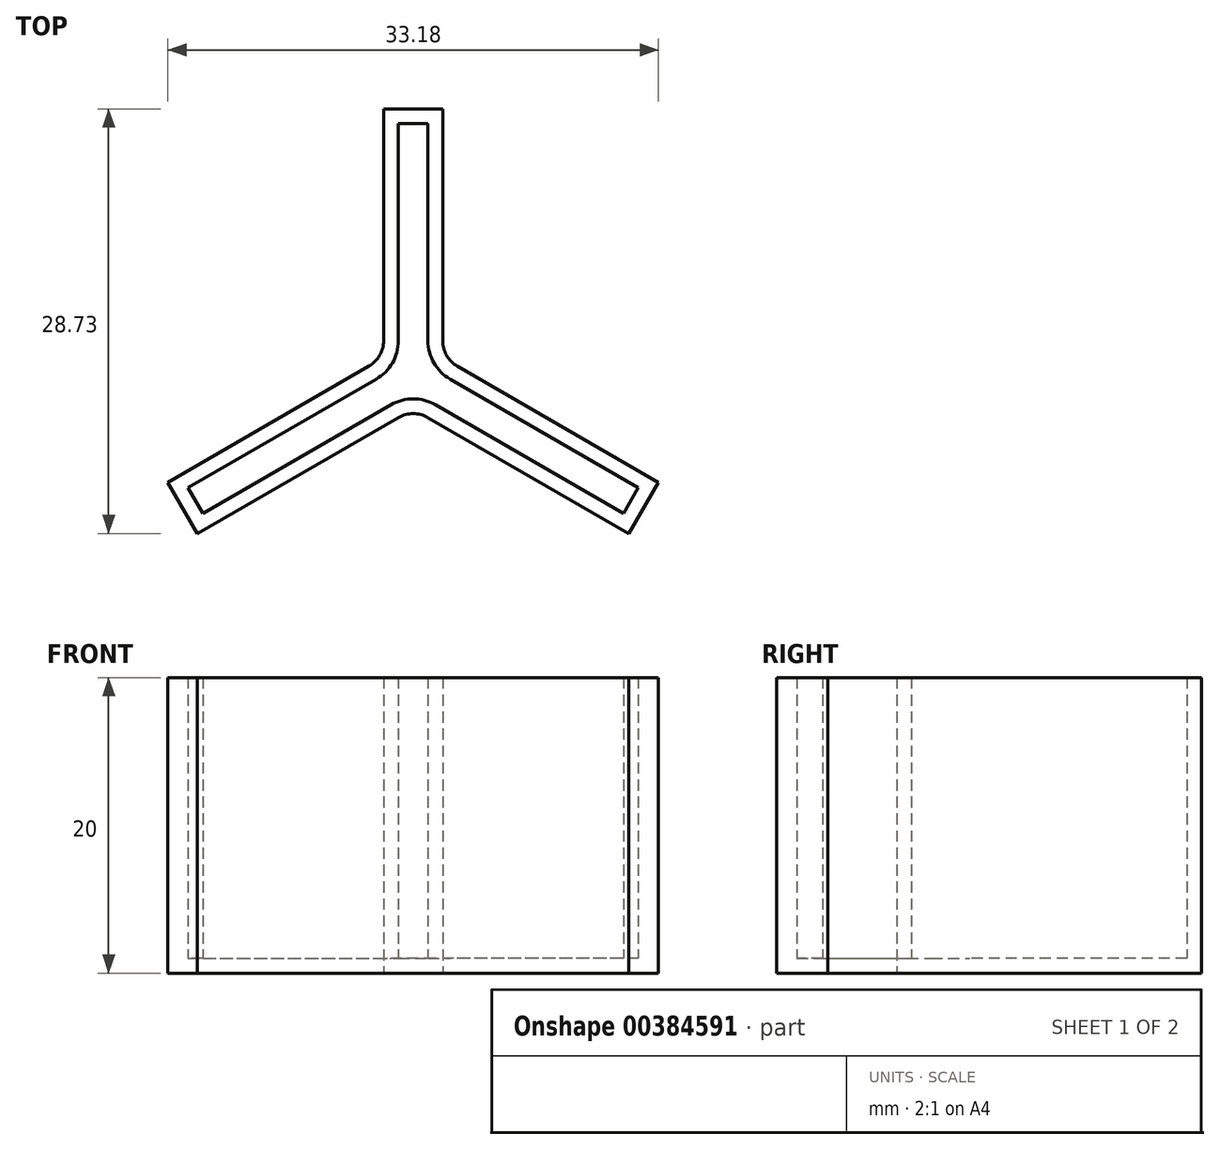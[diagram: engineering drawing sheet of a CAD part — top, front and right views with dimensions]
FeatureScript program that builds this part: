
annotation { "Feature Type Name" : "Feature", "Feature Type Description" : "" }
export const myFeature = defineFeature(function(context is Context, id is Id, definition is map)
    precondition{}
    {
        {
            var Q0;
            Q0=qCreatedBy(makeId("Top.planeOp"),FACE);
            var sketch = newSketch(context, id + "F0", { "sketchPlane" : qUnion([Q0])});
            skLineSegment(sketch, "E0", {"start": v(-1, 17) * mm, "end": v(1, 17) * mm});
            skLineSegment(sketch, "E1", {"start": v(1, 17) * mm, "end": v(1, 2.3) * mm});
            skLineSegment(sketch, "E2.MirrorCS", {"start": v(-1, 17) * mm, "end": v(-1, 2.3) * mm});
            skLineSegment(sketch, "E3.1.0", {"start": v(-14.22, -9.37) * mm, "end": v(-1.5, -2.02) * mm});
            skLineSegment(sketch, "E3.1.1", {"start": v(-14.22, -9.37) * mm, "end": v(-15.22, -7.63) * mm});
            skLineSegment(sketch, "E3.1.2", {"start": v(-15.22, -7.63) * mm, "end": v(-2.5, -0.29) * mm});
            skLineSegment(sketch, "E3.2.0", {"start": v(15.22, -7.63) * mm, "end": v(2.5, -0.29) * mm});
            skLineSegment(sketch, "E3.2.1", {"start": v(15.22, -7.63) * mm, "end": v(14.22, -9.37) * mm});
            skLineSegment(sketch, "E3.2.2", {"start": v(14.22, -9.37) * mm, "end": v(1.5, -2.02) * mm});
            skPoint(sketch, "E3.center", {"position": v(0, 0) * mm});
            skPoint(sketch, "E4.newPointA", {"position": v(-1.5, 2.6) * mm});
            skPoint(sketch, "E4.newPointB", {"position": v(-3, 0) * mm});
            skPoint(sketch, "E5.newPointA", {"position": v(-0.5, 0.87) * mm});
            skPoint(sketch, "E5.newPointB", {"position": v(-1, 0) * mm});
            skArc(sketch, "E5.filletArc", {"start": v(-2.5, -0.29) * mm, "mid": v(-1.4, 0.8) * mm, "end": v(-1, 2.3) * mm});
            skPoint(sketch, "E6.newPointA", {"position": v(1.5, 2.6) * mm});
            skPoint(sketch, "E6.newPointB", {"position": v(3, 0) * mm});
            skPoint(sketch, "E7.newPointA", {"position": v(0.5, 0.87) * mm});
            skPoint(sketch, "E7.newPointB", {"position": v(1, 0) * mm});
            skArc(sketch, "E7.filletArc", {"start": v(1, 2.3) * mm, "mid": v(1.4, 0.8) * mm, "end": v(2.5, -0.29) * mm});
            skPoint(sketch, "E8.newPointA", {"position": v(-0.5, -0.87) * mm});
            skPoint(sketch, "E8.newPointB", {"position": v(0.5, -0.87) * mm});
            skArc(sketch, "E8.filletArc", {"start": v(1.5, -2.02) * mm, "mid": v(0, -1.62) * mm, "end": v(-1.5, -2.02) * mm});
            skPoint(sketch, "E9.newPointA", {"position": v(-1.5, -2.6) * mm});
            skLineSegment(sketch, "E10.0", {"start": v(-14.59, -10.73) * mm, "end": v(-1, -2.89) * mm});
            skArc(sketch, "E11.0", {"start": v(1, -2.89) * mm, "mid": v(0, -2.62) * mm, "end": v(-1, -2.89) * mm});
            skLineSegment(sketch, "E12.0", {"start": v(-14.59, -10.73) * mm, "end": v(-16.59, -7.27) * mm});
            skLineSegment(sketch, "E13.0", {"start": v(-16.59, -7.27) * mm, "end": v(-3, 0.58) * mm});
            skLineSegment(sketch, "E14.1.0", {"start": v(16.59, -7.27) * mm, "end": v(3, 0.58) * mm});
            skLineSegment(sketch, "E14.1.1", {"start": v(16.59, -7.27) * mm, "end": v(14.59, -10.73) * mm});
            skLineSegment(sketch, "E14.1.2", {"start": v(14.59, -10.73) * mm, "end": v(1, -2.89) * mm});
            skArc(sketch, "E14.1.3", {"start": v(2, 2.3) * mm, "mid": v(2.27, 1.3) * mm, "end": v(3, 0.58) * mm});
            skLineSegment(sketch, "E14.2.0", {"start": v(-2, 18) * mm, "end": v(-2, 2.3) * mm});
            skLineSegment(sketch, "E14.2.1", {"start": v(-2, 18) * mm, "end": v(2, 18) * mm});
            skLineSegment(sketch, "E14.2.2", {"start": v(2, 18) * mm, "end": v(2, 2.3) * mm});
            skArc(sketch, "E14.2.3", {"start": v(-3, 0.58) * mm, "mid": v(-2.27, 1.3) * mm, "end": v(-2, 2.3) * mm});
            skSolve(sketch);
        }
        {
            var Q0;
            Q0 = qSketchRegion(id + "F0", true);
            extrude(context, id + "F1", {"entities" : qUnion([Q0]), "depth" : 20 * mm});
        }
        {
            var Q0;
            Q0=makeQuery(id+"F1.opExtrude","CAP_FACE",FACE,{"disambiguationData":[OSD([sQuery(id+"F0.wireOp",EDGE,"E0"),sQuery(id+"F0.wireOp",EDGE,"E1"),sQuery(id+"F0.wireOp",EDGE,"E2.MirrorCS"),sQuery(id+"F0.wireOp",EDGE,"E3.1.0"),sQuery(id+"F0.wireOp",EDGE,"E3.1.1"),sQuery(id+"F0.wireOp",EDGE,"E3.1.2"),sQuery(id+"F0.wireOp",EDGE,"E3.2.0"),sQuery(id+"F0.wireOp",EDGE,"E3.2.1"),sQuery(id+"F0.wireOp",EDGE,"E3.2.2"),sQuery(id+"F0.wireOp",EDGE,"10e7eb02-b686-412f-9961-15af4ba6b5a4.0"),sQuery(id+"F0.wireOp",EDGE,"584127d9-0715-4318-be33-4c08fe5fe5c3.0"),sQuery(id+"F0.wireOp",EDGE,"2b1b5de7-14f9-4f3f-9905-628b27bdaed7.0"),sQuery(id+"F0.wireOp",EDGE,"3dd13835-8f9a-4838-b6b1-501ea5813092.1.0"),sQuery(id+"F0.wireOp",EDGE,"3dd13835-8f9a-4838-b6b1-501ea5813092.1.1"),sQuery(id+"F0.wireOp",EDGE,"3dd13835-8f9a-4838-b6b1-501ea5813092.1.2"),sQuery(id+"F0.wireOp",EDGE,"3dd13835-8f9a-4838-b6b1-501ea5813092.2.0"),sQuery(id+"F0.wireOp",EDGE,"3dd13835-8f9a-4838-b6b1-501ea5813092.2.1"),sQuery(id+"F0.wireOp",EDGE,"3dd13835-8f9a-4838-b6b1-501ea5813092.2.2")])],"isStart":true});
            var sketch = newSketch(context, id + "F2", { "sketchPlane" : qUnion([Q0])});
            skLineSegment(sketch, "E15.0", {"start": v(14.22, 9.37) * mm, "end": v(1.5, 2.02) * mm});
            skLineSegment(sketch, "E16.0", {"start": v(-14.22, 9.37) * mm, "end": v(-1.5, 2.02) * mm});
            skLineSegment(sketch, "E17.0", {"start": v(-15.22, 7.63) * mm, "end": v(-2.5, 0.29) * mm});
            skLineSegment(sketch, "E18.0", {"start": v(-14.22, 9.37) * mm, "end": v(-15.22, 7.63) * mm});
            skLineSegment(sketch, "E19.0", {"start": v(-1, -17) * mm, "end": v(-1, -2.3) * mm});
            skLineSegment(sketch, "E20.0", {"start": v(1, -17) * mm, "end": v(1, -17) * mm});
            skLineSegment(sketch, "E21.0", {"start": v(15.22, 7.63) * mm, "end": v(2.5, 0.29) * mm});
            skLineSegment(sketch, "E22.0", {"start": v(-1, -17) * mm, "end": v(1, -17) * mm});
            skLineSegment(sketch, "E23.0", {"start": v(15.22, 7.63) * mm, "end": v(14.22, 9.37) * mm});
            skArc(sketch, "E24.0", {"start": v(1, -2.3) * mm, "mid": v(1.4, -0.8) * mm, "end": v(2.5, 0.29) * mm});
            skLineSegment(sketch, "E25.0", {"start": v(1, -17) * mm, "end": v(1, -2.3) * mm});
            skArc(sketch, "E26.0", {"start": v(1.5, 2.02) * mm, "mid": v(0, 1.62) * mm, "end": v(-1.5, 2.02) * mm});
            skArc(sketch, "E27.0", {"start": v(-2.5, 0.29) * mm, "mid": v(-1.4, -0.8) * mm, "end": v(-1, -2.3) * mm});
            skSolve(sketch);
        }
        {
            var Q0;
            Q0 = qSketchRegion(id + "F2", true);
            extrude(context, id + "F3", {"entities" : qUnion([Q0]), "operationType" : NewBodyOperationType.ADD, "oppositeDirection" : true, "depth" : 1 * mm});
        }
    });
